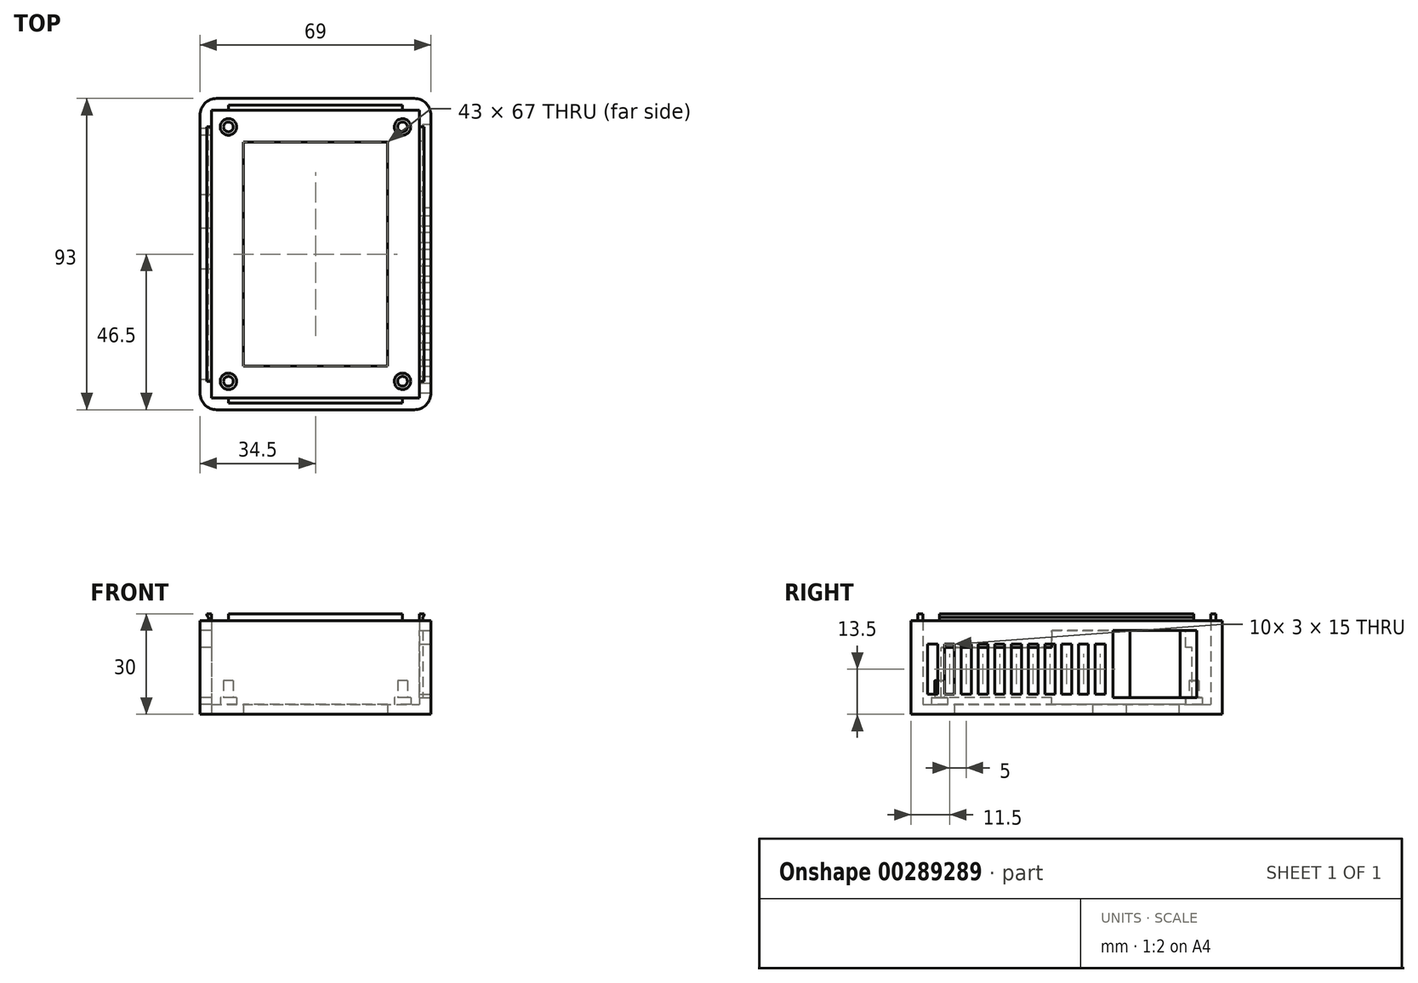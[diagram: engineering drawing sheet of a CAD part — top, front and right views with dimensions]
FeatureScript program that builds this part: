
annotation { "Feature Type Name" : "Feature", "Feature Type Description" : "" }
export const myFeature = defineFeature(function(context is Context, id is Id, definition is map)
    precondition{}
    {
        {
            var Q0;
            Q0=qCreatedBy(makeId("Top.planeOp"),FACE);
            var sketch = newSketch(context, id + "F0", { "sketchPlane" : qUnion([Q0])});
            skLineSegment(sketch, "E0", {"start": v(0, 0) * mm, "end": v(59, 0) * mm});
            skLineSegment(sketch, "E1", {"start": v(59, 0) * mm, "end": v(59, 83) * mm});
            skLineSegment(sketch, "E2", {"start": v(59, 83) * mm, "end": v(0, 83) * mm});
            skLineSegment(sketch, "E3", {"start": v(0, 83) * mm, "end": v(0, 0) * mm});
            skLineSegment(sketch, "E4.0", {"start": v(8, 75) * mm, "end": v(8, 8) * mm});
            skLineSegment(sketch, "E5.0", {"start": v(51, 75) * mm, "end": v(8, 75) * mm});
            skLineSegment(sketch, "E6.0", {"start": v(51, 8) * mm, "end": v(51, 75) * mm});
            skLineSegment(sketch, "E7.0", {"start": v(8, 8) * mm, "end": v(51, 8) * mm});
            skSolve(sketch);
        }
        {
            var Q0;
            Q0 = qSketchRegion(id + "F0", true);
            extrude(context, id + "F1", {"entities" : qUnion([Q0]), "depth" : 3 * mm});
        }
        {
            var Q0;
            Q0=makeQuery(id+"F1.opExtrude","CAP_FACE",FACE,{"disambiguationData":[OSD([sQuery(id+"F0.wireOp",EDGE,"E0"),sQuery(id+"F0.wireOp",EDGE,"E1"),sQuery(id+"F0.wireOp",EDGE,"E2"),sQuery(id+"F0.wireOp",EDGE,"E3"),sQuery(id+"F0.wireOp",EDGE,"E4.0"),sQuery(id+"F0.wireOp",EDGE,"E5.0"),sQuery(id+"F0.wireOp",EDGE,"E6.0"),sQuery(id+"F0.wireOp",EDGE,"E7.0")])],"isStart":false});
            var sketch = newSketch(context, id + "F2", { "sketchPlane" : qUnion([Q0])});
            skCircle(sketch, "E8", {"center": v(3.5, 3.5) * mm, "radius": 1.45 * mm});
            skCircle(sketch, "E9", {"center": v(55.5, 3.5) * mm, "radius": 1.45 * mm});
            skCircle(sketch, "E10", {"center": v(3.5, 79.5) * mm, "radius": 1.45 * mm});
            skCircle(sketch, "E11", {"center": v(55.5, 79.5) * mm, "radius": 1.45 * mm});
            skSolve(sketch);
        }
        {
            var Q0;
            Q0 = qSketchRegion(id + "F2", true);
            extrude(context, id + "F3", {"entities" : qUnion([Q0]), "operationType" : NewBodyOperationType.ADD, "depth" : 7 * mm});
        }
        {
            var Q0;
            Q0=qCreatedBy(makeId("Top.planeOp"),FACE);
            var sketch = newSketch(context, id + "F4", { "sketchPlane" : qUnion([Q0])});
            skLineSegment(sketch, "E12.0", {"start": v(-5, 88) * mm, "end": v(-5, -5) * mm});
            skLineSegment(sketch, "E13.0", {"start": v(64, 88) * mm, "end": v(-5, 88) * mm});
            skLineSegment(sketch, "E14.0", {"start": v(64, -5) * mm, "end": v(64, 88) * mm});
            skLineSegment(sketch, "E15.0", {"start": v(-5, -5) * mm, "end": v(64, -5) * mm});
            skLineSegment(sketch, "E16.bottom", {"start": v(0, 0) * mm, "end": v(59, 0) * mm});
            skLineSegment(sketch, "E16.top", {"start": v(0, 83) * mm, "end": v(59, 83) * mm});
            skLineSegment(sketch, "E16.left", {"start": v(0, 0) * mm, "end": v(0, 83) * mm});
            skLineSegment(sketch, "E16.right", {"start": v(59, 0) * mm, "end": v(59, 83) * mm});
            skSolve(sketch);
        }
        {
            var Q0;
            Q0 = qSketchRegion(id + "F4", true);
            extrude(context, id + "F5", {"entities" : qUnion([Q0]), "operationType" : NewBodyOperationType.ADD, "depth" : 28 * mm});
        }
        {
            var Q0;
            Q0=makeQuery(id+"F1.opExtrude","CAP_FACE",FACE,{"disambiguationData":[OSD([sQuery(id+"F0.wireOp",EDGE,"E0"),sQuery(id+"F0.wireOp",EDGE,"E1"),sQuery(id+"F0.wireOp",EDGE,"E2"),sQuery(id+"F0.wireOp",EDGE,"E3"),sQuery(id+"F0.wireOp",EDGE,"E4.0"),sQuery(id+"F0.wireOp",EDGE,"E5.0"),sQuery(id+"F0.wireOp",EDGE,"E6.0"),sQuery(id+"F0.wireOp",EDGE,"E7.0")])],"isStart":false});
            var sketch = newSketch(context, id + "F6", { "sketchPlane" : qUnion([Q0])});
            skCircle(sketch, "E17.0", {"center": v(3.5, 79.5) * mm, "radius": 2.45 * mm});
            skCircle(sketch, "E18.0", {"center": v(55.5, 79.5) * mm, "radius": 2.45 * mm});
            skCircle(sketch, "E19.0", {"center": v(55.5, 3.5) * mm, "radius": 2.45 * mm});
            skCircle(sketch, "E20.0", {"center": v(3.5, 3.5) * mm, "radius": 2.45 * mm});
            skSolve(sketch);
        }
        {
            var Q0;
            Q0 = qSketchRegion(id + "F6", true);
            extrude(context, id + "F7", {"entities" : qUnion([Q0]), "operationType" : NewBodyOperationType.ADD, "depth" : 2 * mm});
        }
        {
            var Q0;
            Q0=makeQuery(id+"F5.opExtrude","SWEPT_FACE",FACE,{"disambiguationData":[OSD([sQuery(id+"F4.wireOp",EDGE,"E12.0")])]});
            var sketch = newSketch(context, id + "F8", { "sketchPlane" : qUnion([Q0])});
            skLineSegment(sketch, "E21.bottom", {"start": v(-79, 5) * mm, "end": v(-77, 5) * mm});
            skLineSegment(sketch, "E21.top", {"start": v(-79, 20) * mm, "end": v(-77, 20) * mm});
            skLineSegment(sketch, "E21.left", {"start": v(-79, 5) * mm, "end": v(-79, 20) * mm});
            skLineSegment(sketch, "E21.right", {"start": v(-4, 5) * mm, "end": v(-4, 20) * mm});
            skLineSegment(sketch, "E22.bottom", {"start": v(-77, 3) * mm, "end": v(-37, 3) * mm});
            skLineSegment(sketch, "E22.top", {"start": v(-77, 25) * mm, "end": v(-37, 25) * mm});
            skLineSegment(sketch, "E22.left", {"start": v(-77, 3) * mm, "end": v(-77, 5) * mm});
            skLineSegment(sketch, "E22.right", {"start": v(-37, 3) * mm, "end": v(-37, 5) * mm});
            skLineSegment(sketch, "E23.trimOffspring", {"start": v(-37, 20) * mm, "end": v(-4, 20) * mm});
            skLineSegment(sketch, "E24.trimOffspring", {"start": v(-37, 5) * mm, "end": v(-4, 5) * mm});
            skLineSegment(sketch, "E25.trimOffspring", {"start": v(-37, 20) * mm, "end": v(-37, 25) * mm});
            skLineSegment(sketch, "E26.trimOffspring", {"start": v(-77, 20) * mm, "end": v(-77, 25) * mm});
            skSolve(sketch);
        }
        {
            var Q0;
            Q0 = qSketchRegion(id + "F8", true);
            extrude(context, id + "F9", {"entities" : qUnion([Q0]), "operationType" : NewBodyOperationType.REMOVE, "endBound" : BoundingType.UP_TO_NEXT, "oppositeDirection" : true, "depth" : 25 * mm});
        }
        {
            var Q0;
            Q0=makeQuery(id+"F5.opExtrude","SWEPT_FACE",FACE,{"disambiguationData":[OSD([sQuery(id+"F4.wireOp",EDGE,"E14.0")])]});
            var sketch = newSketch(context, id + "F10", { "sketchPlane" : qUnion([Q0])});
            skLineSegment(sketch, "E27.bottom", {"start": v(60.35, 5) * mm, "end": v(75.35, 5) * mm});
            skLineSegment(sketch, "E27.top", {"start": v(60.35, 25) * mm, "end": v(75.35, 25) * mm});
            skLineSegment(sketch, "E27.left", {"start": v(60.35, 5) * mm, "end": v(60.35, 25) * mm});
            skLineSegment(sketch, "E27.right", {"start": v(75.35, 5) * mm, "end": v(75.35, 25) * mm});
            skLineSegment(sketch, "E28.bottom", {"start": v(0, 21) * mm, "end": v(3, 21) * mm});
            skLineSegment(sketch, "E28.top", {"start": v(0, 6) * mm, "end": v(3, 6) * mm});
            skLineSegment(sketch, "E28.left", {"start": v(0, 21) * mm, "end": v(0, 6) * mm});
            skLineSegment(sketch, "E28.right", {"start": v(3, 21) * mm, "end": v(3, 6) * mm});
            skLineSegment(sketch, "E29.1.0.0", {"start": v(5, 21) * mm, "end": v(5, 6) * mm});
            skLineSegment(sketch, "E29.1.0.1", {"start": v(8, 21) * mm, "end": v(8, 6) * mm});
            skLineSegment(sketch, "E29.1.0.2", {"start": v(5, 6) * mm, "end": v(8, 6) * mm});
            skLineSegment(sketch, "E29.1.0.3", {"start": v(5, 21) * mm, "end": v(8, 21) * mm});
            skLineSegment(sketch, "E29.2.0.0", {"start": v(10, 21) * mm, "end": v(10, 6) * mm});
            skLineSegment(sketch, "E29.2.0.1", {"start": v(13, 21) * mm, "end": v(13, 6) * mm});
            skLineSegment(sketch, "E29.2.0.2", {"start": v(10, 6) * mm, "end": v(13, 6) * mm});
            skLineSegment(sketch, "E29.2.0.3", {"start": v(10, 21) * mm, "end": v(13, 21) * mm});
            skLineSegment(sketch, "E29.3.0.0", {"start": v(15, 21) * mm, "end": v(15, 6) * mm});
            skLineSegment(sketch, "E29.3.0.1", {"start": v(18, 21) * mm, "end": v(18, 6) * mm});
            skLineSegment(sketch, "E29.3.0.2", {"start": v(15, 6) * mm, "end": v(18, 6) * mm});
            skLineSegment(sketch, "E29.3.0.3", {"start": v(15, 21) * mm, "end": v(18, 21) * mm});
            skLineSegment(sketch, "E29.4.0.0", {"start": v(20, 21) * mm, "end": v(20, 6) * mm});
            skLineSegment(sketch, "E29.4.0.1", {"start": v(23, 21) * mm, "end": v(23, 6) * mm});
            skLineSegment(sketch, "E29.4.0.2", {"start": v(20, 6) * mm, "end": v(23, 6) * mm});
            skLineSegment(sketch, "E29.4.0.3", {"start": v(20, 21) * mm, "end": v(23, 21) * mm});
            skLineSegment(sketch, "E29.5.0.0", {"start": v(25, 21) * mm, "end": v(25, 6) * mm});
            skLineSegment(sketch, "E29.5.0.1", {"start": v(28, 21) * mm, "end": v(28, 6) * mm});
            skLineSegment(sketch, "E29.5.0.2", {"start": v(25, 6) * mm, "end": v(28, 6) * mm});
            skLineSegment(sketch, "E29.5.0.3", {"start": v(25, 21) * mm, "end": v(28, 21) * mm});
            skLineSegment(sketch, "E29.6.0.0", {"start": v(30, 21) * mm, "end": v(30, 6) * mm});
            skLineSegment(sketch, "E29.6.0.1", {"start": v(33, 21) * mm, "end": v(33, 6) * mm});
            skLineSegment(sketch, "E29.6.0.2", {"start": v(30, 6) * mm, "end": v(33, 6) * mm});
            skLineSegment(sketch, "E29.6.0.3", {"start": v(30, 21) * mm, "end": v(33, 21) * mm});
            skLineSegment(sketch, "E29.7.0.0", {"start": v(35, 21) * mm, "end": v(35, 6) * mm});
            skLineSegment(sketch, "E29.7.0.1", {"start": v(38, 21) * mm, "end": v(38, 6) * mm});
            skLineSegment(sketch, "E29.7.0.2", {"start": v(35, 6) * mm, "end": v(38, 6) * mm});
            skLineSegment(sketch, "E29.7.0.3", {"start": v(35, 21) * mm, "end": v(38, 21) * mm});
            skLineSegment(sketch, "E29.8.0.0", {"start": v(40, 21) * mm, "end": v(40, 6) * mm});
            skLineSegment(sketch, "E29.8.0.1", {"start": v(43, 21) * mm, "end": v(43, 6) * mm});
            skLineSegment(sketch, "E29.8.0.2", {"start": v(40, 6) * mm, "end": v(43, 6) * mm});
            skLineSegment(sketch, "E29.8.0.3", {"start": v(40, 21) * mm, "end": v(43, 21) * mm});
            skLineSegment(sketch, "E29.9.0.0", {"start": v(45, 21) * mm, "end": v(45, 6) * mm});
            skLineSegment(sketch, "E29.9.0.1", {"start": v(48, 21) * mm, "end": v(48, 6) * mm});
            skLineSegment(sketch, "E29.9.0.2", {"start": v(45, 6) * mm, "end": v(48, 6) * mm});
            skLineSegment(sketch, "E29.9.0.3", {"start": v(45, 21) * mm, "end": v(48, 21) * mm});
            skLineSegment(sketch, "E29.10.0.0", {"start": v(50, 21) * mm, "end": v(50, 6) * mm});
            skLineSegment(sketch, "E29.10.0.1", {"start": v(53, 21) * mm, "end": v(53, 6) * mm});
            skLineSegment(sketch, "E29.10.0.2", {"start": v(50, 6) * mm, "end": v(53, 6) * mm});
            skLineSegment(sketch, "E29.10.0.3", {"start": v(50, 21) * mm, "end": v(53, 21) * mm});
            skLineSegment(sketch, "E29.direction1", {"start": v(0, 6) * mm, "end": v(5, 6) * mm, "construction": true});
            skSolve(sketch);
        }
        {
            var Q0;
            Q0 = qSketchRegion(id + "F10", true);
            extrude(context, id + "F11", {"entities" : qUnion([Q0]), "operationType" : NewBodyOperationType.REMOVE, "endBound" : BoundingType.UP_TO_NEXT, "oppositeDirection" : true, "depth" : 25 * mm});
        }
        {
            var Q0;
            Q0=makeQuery(id+"F1.opExtrude","CAP_FACE",FACE,{"disambiguationData":[OSD([sQuery(id+"F0.wireOp",EDGE,"E0"),sQuery(id+"F0.wireOp",EDGE,"E1"),sQuery(id+"F0.wireOp",EDGE,"E2"),sQuery(id+"F0.wireOp",EDGE,"E3"),sQuery(id+"F0.wireOp",EDGE,"E4.0"),sQuery(id+"F0.wireOp",EDGE,"E5.0"),sQuery(id+"F0.wireOp",EDGE,"E6.0"),sQuery(id+"F0.wireOp",EDGE,"E7.0")])],"isStart":false});
            var sketch = newSketch(context, id + "F12", { "sketchPlane" : qUnion([Q0])});
            skLineSegment(sketch, "E30.bottom", {"start": v(-1.5, -1.5) * mm, "end": v(60.5, -1.5) * mm});
            skLineSegment(sketch, "E30.top", {"start": v(-1.5, 84.5) * mm, "end": v(60.5, 84.5) * mm});
            skLineSegment(sketch, "E30.left", {"start": v(-1.5, -1.5) * mm, "end": v(-1.5, 84.5) * mm});
            skLineSegment(sketch, "E30.right", {"start": v(60.5, -1.5) * mm, "end": v(60.5, 84.5) * mm});
            skCircle(sketch, "E31", {"center": v(3.5, 79.5) * mm, "radius": 2.5 * mm});
            skCircle(sketch, "E32", {"center": v(55.5, 79.5) * mm, "radius": 2.5 * mm});
            skCircle(sketch, "E33", {"center": v(55.5, 3.5) * mm, "radius": 2.5 * mm});
            skCircle(sketch, "E34", {"center": v(3.5, 3.5) * mm, "radius": 2.5 * mm});
            skSolve(sketch);
        }
        {
            var Q0;
            Q0 = qSketchRegion(id + "F12", true);
            extrude(context, id + "F13", {"entities" : qUnion([Q0]), "operationType" : NewBodyOperationType.REMOVE, "depth" : 25 * mm});
        }
        {
            var Q0;
            Q0=makeQuery(id+"F13.boolean.opBoolean","COPY",FACE,{"derivedFrom":makeQuery(id+"F13.opExtrude","SWEPT_FACE",FACE,{"disambiguationData":[OSD([sQuery(id+"F12.wireOp",EDGE,"E30.top")])]})});
            cPlane(context, id + "F14", {"entities" : qUnion([Q0]), "cplaneType" : CPlaneType.OFFSET, "offset" : 5 * mm, "width" : 150 * mm, "height" : 150 * mm});
        }
        {
            var Q0;
            Q0=makeQuery(id+"F5.opExtrude","SWEPT_FACE",FACE,{"disambiguationData":[OSD([sQuery(id+"F4.wireOp",EDGE,"E12.0")])]});
            var sketch = newSketch(context, id + "F15", { "sketchPlane" : qUnion([Q0])});
            skLineSegment(sketch, "E35.bottom", {"start": v(-59.22, 3) * mm, "end": v(-49.22, 3) * mm});
            skLineSegment(sketch, "E35.top", {"start": v(-59.22, 0) * mm, "end": v(-49.22, 0) * mm});
            skLineSegment(sketch, "E35.left", {"start": v(-59.22, 3) * mm, "end": v(-59.22, 0) * mm});
            skLineSegment(sketch, "E35.right", {"start": v(-49.22, 3) * mm, "end": v(-49.22, 0) * mm});
            skSolve(sketch);
        }
        {
            var Q0;
            Q0=makeQuery(id+"F15.imprint","IMPRINT",FACE,{"disambiguationData":[TD([[makeQuery(id+"F15.imprint","IMPRINT",EDGE,{"derivedFrom":sQuery(id+"F15.wireOp",EDGE,"E35.bottom")}),-1.0]])]});
            extrude(context, id + "F16", {"entities" : qUnion([Q0]), "operationType" : NewBodyOperationType.REMOVE, "oppositeDirection" : true, "depth" : 3.5 * mm});
        }
        {
            var Q0;
            Q0=makeQuery(id+"F5.opExtrude","SWEPT_FACE",FACE,{"disambiguationData":[OSD([sQuery(id+"F4.wireOp",EDGE,"E14.0")])]});
            var sketch = newSketch(context, id + "F17", { "sketchPlane" : qUnion([Q0])});
            skLineSegment(sketch, "E36.bottom", {"start": v(55.35, 25) * mm, "end": v(80.35, 25) * mm});
            skLineSegment(sketch, "E36.top", {"start": v(55.35, 5) * mm, "end": v(80.35, 5) * mm});
            skLineSegment(sketch, "E36.left", {"start": v(55.35, 25) * mm, "end": v(55.35, 5) * mm});
            skLineSegment(sketch, "E36.right", {"start": v(80.35, 25) * mm, "end": v(80.35, 5) * mm});
            skSolve(sketch);
        }
        {
            var Q0;
            Q0 = qSketchRegion(id + "F17", true);
            extrude(context, id + "F18", {"entities" : qUnion([Q0]), "operationType" : NewBodyOperationType.REMOVE, "oppositeDirection" : true, "depth" : 2.5 * mm});
        }
        {
            var Q0;
            Q0=makeQuery(id+"F21.boolean.opBoolean","MERGE",FACE,{"derivedFrom":[makeQuery(id+"F13.boolean.opBoolean","COPY",FACE,{"derivedFrom":makeQuery(id+"F13.opExtrude","SWEPT_FACE",FACE,{"disambiguationData":[OSD([sQuery(id+"F12.wireOp",EDGE,"E30.left")])]})}),makeQuery(id+"F21.opExtrude","SWEPT_FACE",FACE,{"disambiguationData":[OSD([sQuery(id+"F20.wireOp",EDGE,"E40")])]})]});
            cPlane(context, id + "F19", {"entities" : qUnion([Q0]), "cplaneType" : CPlaneType.OFFSET, "offset" : (62 / 2) * mm, "width" : 150 * mm, "height" : 150 * mm});
        }
        {
            var Q0;
            Q0=qCreatedBy(id+"F14.planeOp",FACE);
            var sketch = newSketch(context, id + "F20", { "sketchPlane" : qUnion([Q0])});
            skLineSegment(sketch, "E37.0.1", {"start": v(-5, 28) * mm, "end": v(-1.5, 28) * mm});
            skLineSegment(sketch, "E37.0.3", {"start": v(64, 28) * mm, "end": v(60.5, 28) * mm});
            skLineSegment(sketch, "E38.0.1", {"start": v(60.5, 3) * mm, "end": v(60.5, 28) * mm});
            skLineSegment(sketch, "E38.0.3", {"start": v(60.5, 28) * mm, "end": v(60.5, 3) * mm});
            skLineSegment(sketch, "E39.0.0", {"start": v(-1.5, 5) * mm, "end": v(-1.5, 3) * mm});
            skLineSegment(sketch, "E39.0.2", {"start": v(-1.5, 3) * mm, "end": v(-1.5, 28) * mm});
            skLineSegment(sketch, "E39.0.4", {"start": v(-1.5, 25) * mm, "end": v(-1.5, 3) * mm});
            skLineSegment(sketch, "E39.0.6", {"start": v(-1.5, 3) * mm, "end": v(-1.5, 5) * mm});
            skLineSegment(sketch, "E39.0.8", {"start": v(-1.5, 5) * mm, "end": v(-1.5, 20) * mm});
            skLineSegment(sketch, "E39.0.10", {"start": v(-1.5, 20) * mm, "end": v(-1.5, 25) * mm});
            skLineSegment(sketch, "E39.0.12", {"start": v(-1.5, 25) * mm, "end": v(-1.5, 20) * mm});
            skLineSegment(sketch, "E39.0.14", {"start": v(-1.5, 20) * mm, "end": v(-1.5, 5) * mm});
            skLineSegment(sketch, "E40", {"start": v(-1.5, 28) * mm, "end": v(-1.5, 30) * mm});
            skLineSegment(sketch, "E41", {"start": v(-1.5, 30) * mm, "end": v(-3, 30) * mm});
            skLineSegment(sketch, "E42", {"start": v(-2.5, 28) * mm, "end": v(-2.5, 29) * mm});
            skArc(sketch, "E43", {"start": v(-3, 30) * mm, "mid": v(-2.87, 29.44) * mm, "end": v(-2.5, 29) * mm});
            skPoint(sketch, "E44.orphan", {"position": v(-5, 28) * mm});
            skLineSegment(sketch, "E45.trimOffspring", {"start": v(-1.5, 28) * mm, "end": v(-2.5, 28) * mm});
            skLineSegment(sketch, "E46.trimOffspring", {"start": v(60.5, 28) * mm, "end": v(64, 28) * mm});
            skLineSegment(sketch, "E47.MirrorCS", {"start": v(60.5, 28) * mm, "end": v(61.5, 28) * mm});
            skLineSegment(sketch, "E48.MirrorCS", {"start": v(60.5, 28) * mm, "end": v(60.5, 30) * mm});
            skLineSegment(sketch, "E49.MirrorCS", {"start": v(60.5, 30) * mm, "end": v(62, 30) * mm});
            skLineSegment(sketch, "E50.MirrorCS", {"start": v(61.5, 28) * mm, "end": v(61.5, 29) * mm});
            skArc(sketch, "E51.MirrorCS", {"start": v(62, 30) * mm, "mid": v(61.87, 29.44) * mm, "end": v(61.5, 29) * mm});
            skSolve(sketch);
        }
        {
            var Q0;
            Q0 = qSketchRegion(id + "F20", true);
            extrude(context, id + "F21", {"entities" : qUnion([Q0]), "operationType" : NewBodyOperationType.ADD, "depth" : 76 * mm});
        }
        {
            var Q0;
            Q0=makeQuery(id+"F21.boolean.opBoolean","MERGE",FACE,{"derivedFrom":[makeQuery(id+"F13.boolean.opBoolean","COPY",FACE,{"derivedFrom":makeQuery(id+"F13.opExtrude","SWEPT_FACE",FACE,{"disambiguationData":[OSD([sQuery(id+"F12.wireOp",EDGE,"E30.left")])]})}),makeQuery(id+"F21.opExtrude","SWEPT_FACE",FACE,{"disambiguationData":[OSD([sQuery(id+"F20.wireOp",EDGE,"E40")])]})]});
            cPlane(context, id + "F22", {"entities" : qUnion([Q0]), "cplaneType" : CPlaneType.OFFSET, "offset" : 5 * mm, "width" : 150 * mm, "height" : 150 * mm});
        }
        {
            var Q0;
            Q0=qCreatedBy(id+"F22.planeOp",FACE);
            var sketch = newSketch(context, id + "F23", { "sketchPlane" : qUnion([Q0])});
            skLineSegment(sketch, "E52.0.1", {"start": v(84.5, 3) * mm, "end": v(84.5, 28) * mm});
            skLineSegment(sketch, "E52.0.3", {"start": v(84.5, 28) * mm, "end": v(84.5, 3) * mm});
            skLineSegment(sketch, "E53.0.1", {"start": v(-1.5, 3) * mm, "end": v(-1.5, 28) * mm});
            skLineSegment(sketch, "E53.0.3", {"start": v(-1.5, 28) * mm, "end": v(-1.5, 3) * mm});
            skLineSegment(sketch, "E54.bottom", {"start": v(-1.5, 28) * mm, "end": v(-3, 28) * mm});
            skLineSegment(sketch, "E54.top", {"start": v(-1.5, 30) * mm, "end": v(-3, 30) * mm});
            skLineSegment(sketch, "E54.left", {"start": v(-1.5, 28) * mm, "end": v(-1.5, 30) * mm});
            skLineSegment(sketch, "E54.right", {"start": v(-3, 28) * mm, "end": v(-3, 30) * mm});
            skLineSegment(sketch, "E55.bottom", {"start": v(84.5, 28) * mm, "end": v(86, 28) * mm});
            skLineSegment(sketch, "E55.top", {"start": v(84.5, 30) * mm, "end": v(86, 30) * mm});
            skLineSegment(sketch, "E55.left", {"start": v(84.5, 28) * mm, "end": v(84.5, 30) * mm});
            skLineSegment(sketch, "E55.right", {"start": v(86, 28) * mm, "end": v(86, 30) * mm});
            skSolve(sketch);
        }
        {
            var Q0;
            Q0 = qSketchRegion(id + "F23", true);
            extrude(context, id + "F24", {"entities" : qUnion([Q0]), "operationType" : NewBodyOperationType.ADD, "depth" : 52 * mm});
        }
        {
            var Q0;
            Q0=makeQuery(id+"F5.opExtrude","SWEPT_EDGE",EDGE,{"disambiguationData":[OSD([sQuery(id+"F4.wireOp",EDGE,"E12.0"),sQuery(id+"F4.wireOp",EDGE,"E15.0")])]});
            var Q1;
            Q1=makeQuery(id+"F5.opExtrude","SWEPT_EDGE",EDGE,{"disambiguationData":[OSD([sQuery(id+"F4.wireOp",EDGE,"E14.0"),sQuery(id+"F4.wireOp",EDGE,"E15.0")])]});
            var Q2;
            Q2=makeQuery(id+"F5.opExtrude","SWEPT_EDGE",EDGE,{"disambiguationData":[OSD([sQuery(id+"F4.wireOp",EDGE,"E13.0"),sQuery(id+"F4.wireOp",EDGE,"E14.0")])]});
            var Q3;
            Q3=makeQuery(id+"F5.opExtrude","SWEPT_EDGE",EDGE,{"disambiguationData":[OSD([sQuery(id+"F4.wireOp",EDGE,"E12.0"),sQuery(id+"F4.wireOp",EDGE,"E13.0")])]});
            fillet(context, id + "F25", {"entities" : qUnion([Q0, Q1, Q2, Q3]), "radius" : 5 * mm, "tangentPropagation" : true, "allowEdgeOverflow" : false});
        }
    });
